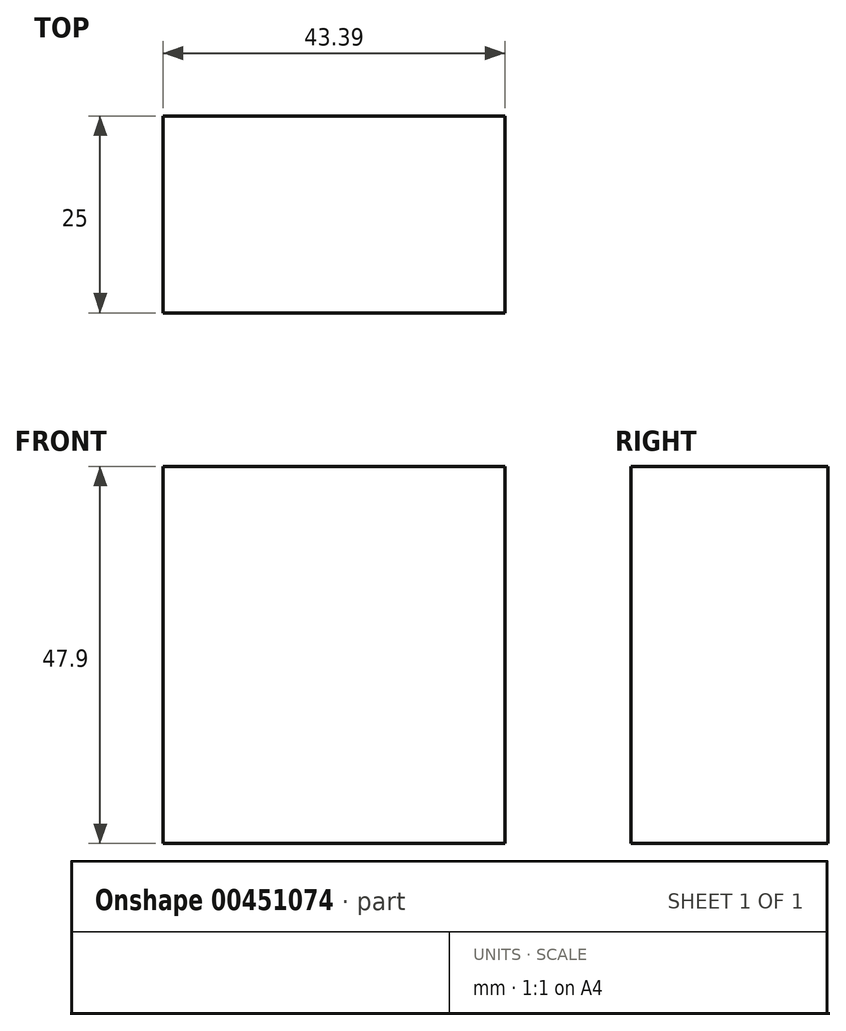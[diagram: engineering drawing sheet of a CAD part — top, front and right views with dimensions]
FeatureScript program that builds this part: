
annotation { "Feature Type Name" : "Feature", "Feature Type Description" : "" }
export const myFeature = defineFeature(function(context is Context, id is Id, definition is map)
    precondition{}
    {
        {
            var Q0;
            Q0=qCreatedBy(makeId("Front.planeOp"),FACE);
            var sketch = newSketch(context, id + "F0", { "sketchPlane" : qUnion([Q0])});
            skLineSegment(sketch, "E0.bottom", {"start": v(-122, -10.18) * mm, "end": v(-78.6, -10.18) * mm});
            skLineSegment(sketch, "E0.top", {"start": v(-122, 37.72) * mm, "end": v(-78.6, 37.72) * mm});
            skLineSegment(sketch, "E0.left", {"start": v(-122, -10.18) * mm, "end": v(-122, 37.72) * mm});
            skLineSegment(sketch, "E0.right", {"start": v(-78.6, -10.18) * mm, "end": v(-78.6, 37.72) * mm});
            skPoint(sketch, "E0.middle", {"position": v(-100.3, 13.77) * mm});
            skSolve(sketch);
        }
        {
            var Q0;
            Q0=makeQuery(id+"F0.imprint","IMPRINT",FACE,{"disambiguationData":[TD([[makeQuery(id+"F0.imprint","IMPRINT",EDGE,{"derivedFrom":sQuery(id+"F0.wireOp",EDGE,"E0.bottom")}),1.0]])]});
            extrude(context, id + "F1", {"entities" : qUnion([Q0]), "depth" : 25 * mm});
        }
    });
